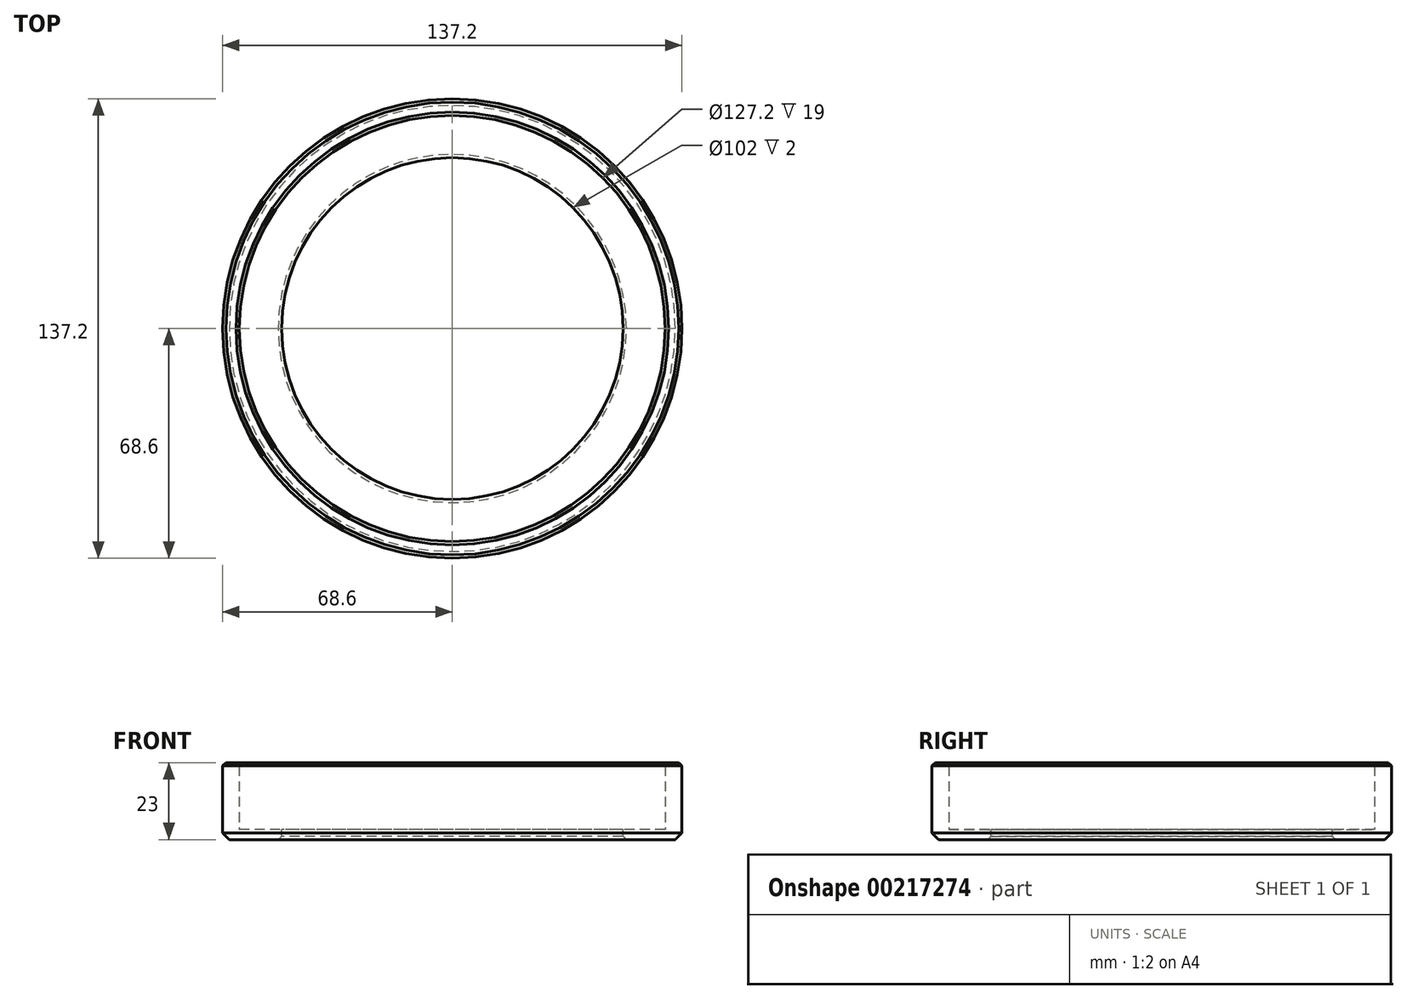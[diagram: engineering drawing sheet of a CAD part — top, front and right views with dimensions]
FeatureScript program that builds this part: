
annotation { "Feature Type Name" : "Feature", "Feature Type Description" : "" }
export const myFeature = defineFeature(function(context is Context, id is Id, definition is map)
    precondition{}
    {
        {
            var Q0;
            Q0=qCreatedBy(makeId("Top.planeOp"),FACE);
            var sketch = newSketch(context, id + "F0", { "sketchPlane" : qUnion([Q0])});
            skCircle(sketch, "E0", {"center": v(0, 0) * mm, "radius": 68.6 * mm});
            skCircle(sketch, "E1", {"center": v(0, 0) * mm, "radius": 63.6 * mm});
            skSolve(sketch);
        }
        {
            var Q0;
            Q0=qSketchRegion(id+"F0",true);
            extrude(context, id + "F1", {"entities" : qUnion([Q0]), "depth" : 20 * mm});
        }
        {
            var Q0;
            Q0=qCreatedBy(makeId("Top.planeOp"),FACE);
            var sketch = newSketch(context, id + "F2", { "sketchPlane" : qUnion([Q0])});
            skCircle(sketch, "E2", {"center": v(0, 0) * mm, "radius": 51 * mm});
            skCircle(sketch, "E3", {"center": v(0, 0) * mm, "radius": 68.6 * mm});
            skSolve(sketch);
        }
        {
            var Q0;
            Q0=qSketchRegion(id+"F2",true);
            extrude(context, id + "F3", {"entities" : qUnion([Q0]), "operationType" : NewBodyOperationType.ADD, "oppositeDirection" : true, "depth" : 3 * mm});
        }
        {
            var Q0;
            Q0=makeQuery(id+"F3.opExtrude","CAP_EDGE",EDGE,{"disambiguationData":[OSD([sQuery(id+"F2.wireOp",EDGE,"E3")])],"isStart":false});
            chamfer(context, id + "F4", {"entities" : qUnion([Q0]), "width" : 2 * mm, "tangentPropagation" : true});
        }
        {
            var Q0;
            Q0=makeQuery(id+"F3.opExtrude","CAP_EDGE",EDGE,{"disambiguationData":[OSD([sQuery(id+"F2.wireOp",EDGE,"E2")])],"isStart":false});
            var Q1;
            Q1=makeQuery(id+"F1.opExtrude","CAP_EDGE",EDGE,{"disambiguationData":[OSD([sQuery(id+"F0.wireOp",EDGE,"E1")])],"isStart":false});
            var Q2;
            Q2=makeQuery(id+"F1.opExtrude","CAP_EDGE",EDGE,{"disambiguationData":[OSD([sQuery(id+"F0.wireOp",EDGE,"E0")])],"isStart":false});
            chamfer(context, id + "F5", {"entities" : qUnion([Q0, Q1, Q2]), "width" : 1 * mm, "tangentPropagation" : true});
        }
    });
